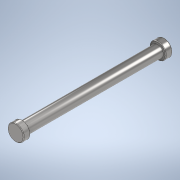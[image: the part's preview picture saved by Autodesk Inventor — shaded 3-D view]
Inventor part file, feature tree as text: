
AUTODESK INVENTOR PART (.ipt)
format: ipt  version: 2021 (Build 250183000, 183)  size: 124,928 bytes
history: native  units: mm
features: extrude x2, sketch x2, mirror x1, fillet x1
ambient origin geometry x8: Origin, YZ Plane, XZ Plane, XY Plane, X Axis, Y Axis, Z Axis, Center Point
bodies: Solid1 (feature_tree)
feature tree (6):
  extrude  "Extrusion1"  Depth=100.0mm TaperAngle=0.0deg
  extrude  "Extrusion2"  Depth=5.0mm TaperAngle=0.0deg
  mirror  "Mirror1"
  fillet  "Fillet1"  Radius=0.5mm
  sketch  "Sketch1"  dims[d0=8.5mm d1=100.0mm d2=0.0mm]
  sketch  "Sketch2"  dims[d3=12.0mm d4=5.0mm d5=0.0mm d6=0.5mm]
